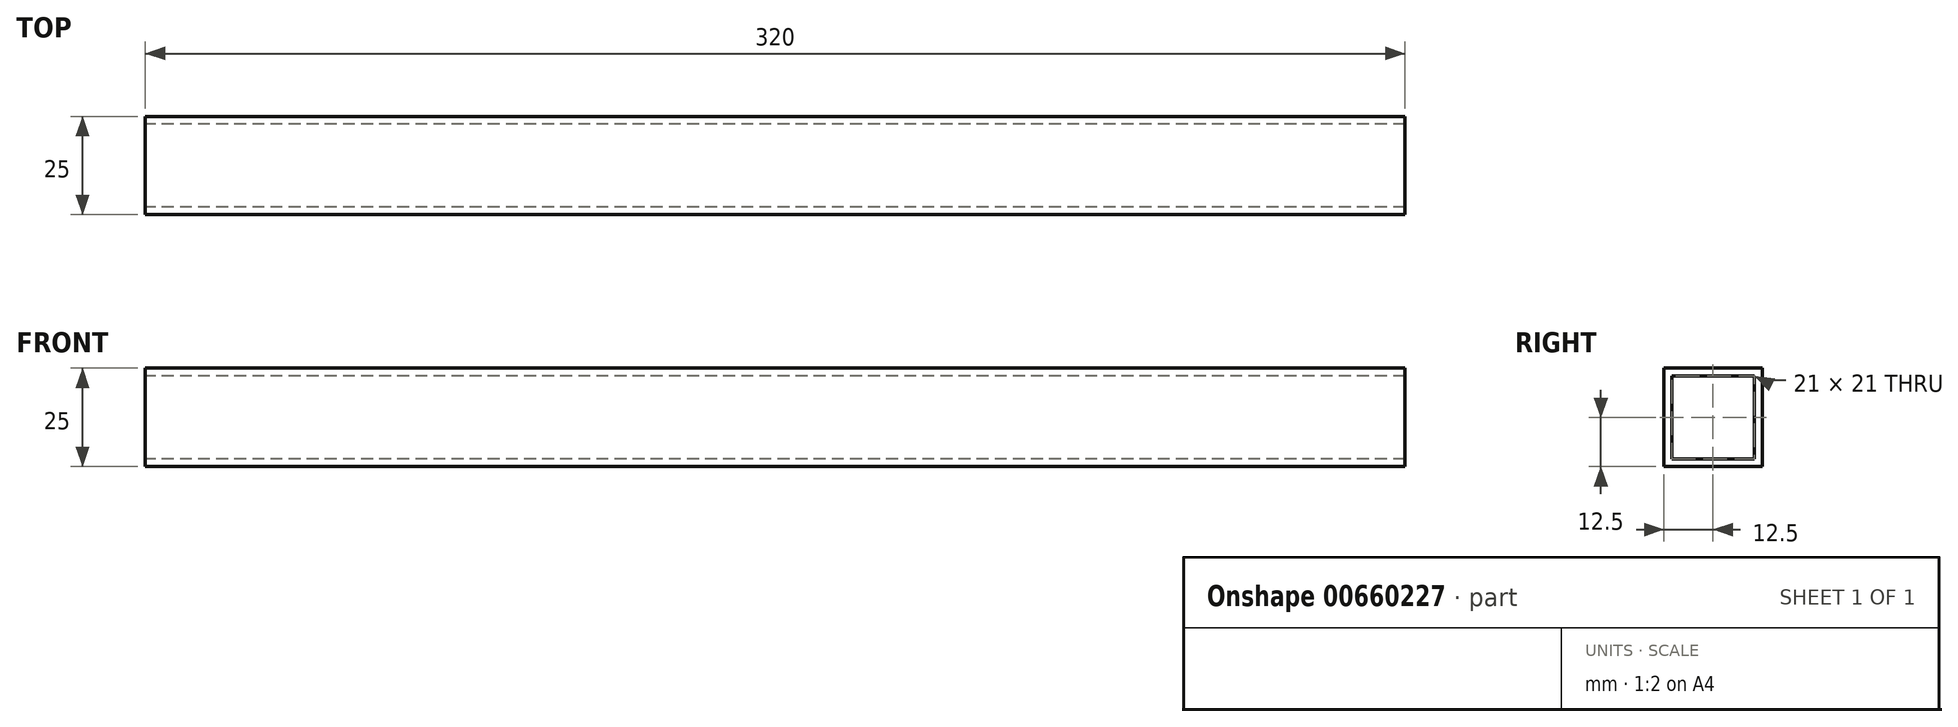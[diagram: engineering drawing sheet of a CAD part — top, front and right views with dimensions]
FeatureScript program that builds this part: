
annotation { "Feature Type Name" : "Feature", "Feature Type Description" : "" }
export const myFeature = defineFeature(function(context is Context, id is Id, definition is map)
    precondition{}
    {
        {
            var Q0;
            Q0=qCreatedBy(makeId("Right.planeOp"),FACE);
            var sketch = newSketch(context, id + "F0", { "sketchPlane" : qUnion([Q0])});
            skLineSegment(sketch, "E0.bottom", {"start": v(-12.5, 12.5) * mm, "end": v(12.5, 12.5) * mm});
            skLineSegment(sketch, "E0.top", {"start": v(-12.5, -12.5) * mm, "end": v(12.5, -12.5) * mm});
            skLineSegment(sketch, "E0.left", {"start": v(-12.5, 12.5) * mm, "end": v(-12.5, -12.5) * mm});
            skLineSegment(sketch, "E0.right", {"start": v(12.5, 12.5) * mm, "end": v(12.5, -12.5) * mm});
            skLineSegment(sketch, "E1.bottom", {"start": v(-10.5, 10.5) * mm, "end": v(10.5, 10.5) * mm});
            skLineSegment(sketch, "E1.top", {"start": v(-10.5, -10.5) * mm, "end": v(10.5, -10.5) * mm});
            skLineSegment(sketch, "E1.left", {"start": v(-10.5, 10.5) * mm, "end": v(-10.5, -10.5) * mm});
            skLineSegment(sketch, "E1.right", {"start": v(10.5, 10.5) * mm, "end": v(10.5, -10.5) * mm});
            skSolve(sketch);
        }
        {
            var Q0;
            Q0 = qSketchRegion(id + "F0", true);
            extrude(context, id + "F1", {"entities" : qUnion([Q0]), "endBound" : BoundingType.SYMMETRIC, "depth" : 320 * mm, "offsetDistance" : 25 * mm});
        }
    });
